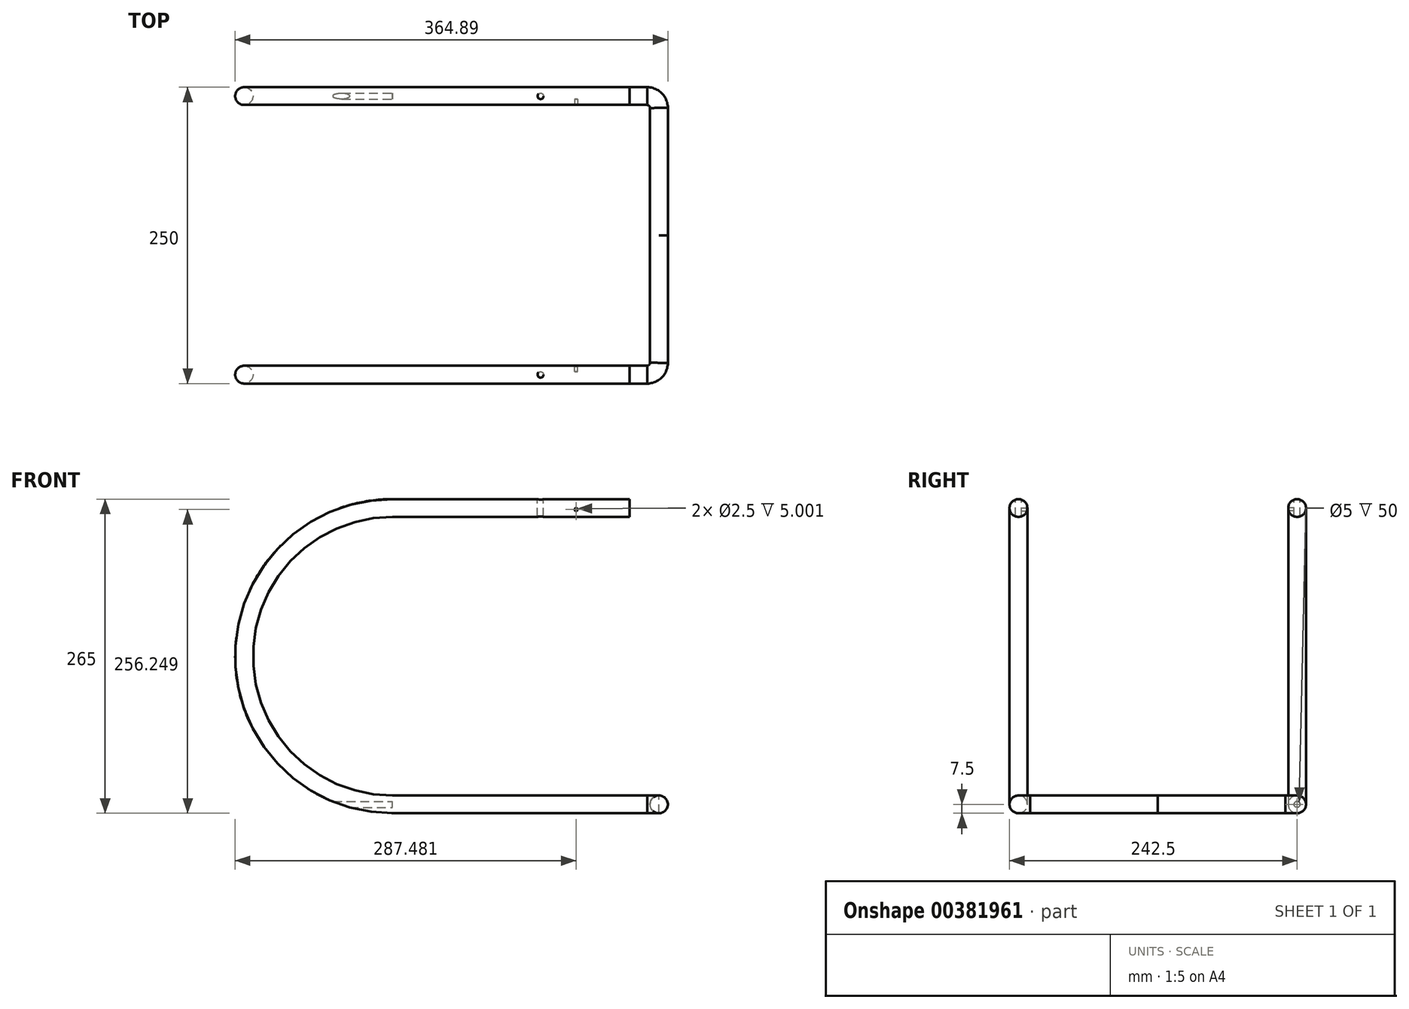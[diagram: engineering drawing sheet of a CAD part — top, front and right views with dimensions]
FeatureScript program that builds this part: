
annotation { "Feature Type Name" : "Feature", "Feature Type Description" : "" }
export const myFeature = defineFeature(function(context is Context, id is Id, definition is map)
    precondition{}
    {
        {
            var Q0;
            Q0=qCreatedBy(makeId("Front.planeOp"),FACE);
            var sketch = newSketch(context, id + "F0", { "sketchPlane" : qUnion([Q0])});
            skLineSegment(sketch, "E0", {"start": v(0, 0) * mm, "end": v(215, 0) * mm});
            skArc(sketch, "E1", {"start": v(0, 250) * mm, "mid": v(-125, 125) * mm, "end": v(0, 0) * mm});
            skLineSegment(sketch, "E2", {"start": v(0, 250) * mm, "end": v(200, 250) * mm});
            skSolve(sketch);
        }
        {
            var Q0;
            Q0=qCreatedBy(makeId("Top.planeOp"),FACE);
            var sketch = newSketch(context, id + "F1", { "sketchPlane" : qUnion([Q0])});
            skLineSegment(sketch, "E3", {"start": v(224.89, -10) * mm, "end": v(224.89, -117.5) * mm});
            skArc(sketch, "E4", {"start": v(224.89, -10) * mm, "mid": v(221.96, -2.93) * mm, "end": v(214.89, 0) * mm});
            skSolve(sketch);
        }
        {
            var Q0;
            Q0=qCreatedBy(makeId("Right.planeOp"),FACE);
            cPlane(context, id + "F2", {"entities" : qUnion([Q0]), "cplaneType" : CPlaneType.OFFSET, "offset" : 215 * mm, "width" : 150 * mm, "height" : 150 * mm});
        }
        {
            var Q0;
            Q0=qCreatedBy(id+"F2.planeOp",FACE);
            var sketch = newSketch(context, id + "F3", { "sketchPlane" : qUnion([Q0])});
            skCircle(sketch, "E5", {"center": v(0, 0) * mm, "radius": 7.5 * mm});
            skSolve(sketch);
        }
        {
            var Q0;
            Q0=makeQuery(id+"F3.imprint","IMPRINT",FACE,{"disambiguationData":[TD([[makeQuery(id+"F3.imprint","IMPRINT",EDGE,{"derivedFrom":sQuery(id+"F3.wireOp",EDGE,"E5")}),1.0]])]});
            var Q1;
            Q1=sQuery(id+"F0.wireOp",EDGE,"E0");
            var Q2;
            Q2=sQuery(id+"F0.wireOp",EDGE,"E1");
            var Q3;
            Q3=sQuery(id+"F0.wireOp",EDGE,"E2");
            sweep(context, id + "F4", {"profiles" : qUnion([Q0]), "path" : qUnion([Q1, Q2, Q3])});
        }
        {
            var Q0;
            Q0=makeQuery(id+"F4.opSweep","CAP_FACE",FACE,{"disambiguationData":[OSD([sQuery(id+"F0.wireOp",VERTEX,"E0.end"),sQuery(id+"F3.wireOp",EDGE,"E5")])],"isStart":true});
            var Q1;
            Q1=sQuery(id+"F1.wireOp",EDGE,"E4");
            var Q2;
            Q2=sQuery(id+"F1.wireOp",EDGE,"E3");
            sweep(context, id + "F5", {"operationType" : NewBodyOperationType.ADD, "profiles" : qUnion([Q0]), "path" : qUnion([Q1, Q2])});
        }
        {
            var Q0;
            Q0=qCreatedBy(makeId("Front.planeOp"),FACE);
            cPlane(context, id + "F6", {"entities" : qUnion([Q0]), "cplaneType" : CPlaneType.OFFSET, "offset" : 117.5 * mm, "width" : 150 * mm, "height" : 150 * mm});
        }
        {
            var Q0;
            Q0=qCreatedBy(makeId("Front.planeOp"),FACE);
            cPlane(context, id + "F7", {"entities" : qUnion([Q0]), "cplaneType" : CPlaneType.OFFSET, "offset" : 7.5 * mm, "width" : 150 * mm, "height" : 150 * mm});
        }
        {
            var Q0;
            Q0=qCreatedBy(id+"F7.planeOp",FACE);
            var sketch = newSketch(context, id + "F8", { "sketchPlane" : qUnion([Q0])});
            skCircle(sketch, "E6", {"center": v(154.98, 248.75) * mm, "radius": 1.25 * mm});
            skSolve(sketch);
        }
        {
            var Q0;
            Q0=qSketchRegion(id+"F8",true);
            extrude(context, id + "F9", {"entities" : qUnion([Q0]), "operationType" : NewBodyOperationType.REMOVE, "oppositeDirection" : true, "depth" : 5 * mm});
        }
        {
            var Q0;
            Q0=makeQuery(id+"F4.opSweep","SWEPT_BODY",BODY,{"disambiguationData":[OSD([sQuery(id+"F0.wireOp",EDGE,"E2"),sQuery(id+"F3.wireOp",EDGE,"E5")])]});
            var Q1;
            Q1=qCreatedBy(id+"F6.planeOp",FACE);
            mirror(context, id + "F10", {"operationType" : NewBodyOperationType.ADD, "entities" : qUnion([Q0]), "mirrorPlane" : qUnion([Q1])});
        }
        {
            var Q0;
            Q0=qCreatedBy(makeId("Right.planeOp"),FACE);
            var sketch = newSketch(context, id + "F11", { "sketchPlane" : qUnion([Q0])});
            skCircle(sketch, "E7", {"center": v(0, 0) * mm, "radius": 2.5 * mm});
            skSolve(sketch);
        }
        {
            var Q0;
            Q0=qSketchRegion(id+"F11",true);
            extrude(context, id + "F12", {"entities" : qUnion([Q0]), "operationType" : NewBodyOperationType.REMOVE, "oppositeDirection" : true, "depth" : 30 * mm});
        }
        {
            var Q0;
            Q0=qCreatedBy(makeId("Right.planeOp"),FACE);
            var sketch = newSketch(context, id + "F13", { "sketchPlane" : qUnion([Q0])});
            skCircle(sketch, "E8", {"center": v(0, 0) * mm, "radius": 2.5 * mm});
            skSolve(sketch);
        }
        {
            var Q0;
            Q0=qSketchRegion(id+"F13",true);
            extrude(context, id + "F14", {"entities" : qUnion([Q0]), "operationType" : NewBodyOperationType.REMOVE, "oppositeDirection" : true, "depth" : 50 * mm});
        }
        {
            var Q0;
            Q0=qCreatedBy(makeId("Top.planeOp"),FACE);
            cPlane(context, id + "F15", {"entities" : qUnion([Q0]), "cplaneType" : CPlaneType.OFFSET, "offset" : 257.5 * mm, "width" : 150 * mm, "height" : 150 * mm});
        }
        {
            var Q0;
            Q0=qCreatedBy(id+"F15.planeOp",FACE);
            var sketch = newSketch(context, id + "F16", { "sketchPlane" : qUnion([Q0])});
            skCircle(sketch, "E9", {"center": v(125, 0) * mm, "radius": 2.5 * mm});
            skCircle(sketch, "E10", {"center": v(125, -235) * mm, "radius": 2.5 * mm});
            skSolve(sketch);
        }
        {
            var Q0;
            Q0=makeQuery(id+"F16.imprint","IMPRINT",FACE,{"disambiguationData":[TD([[makeQuery(id+"F16.imprint","IMPRINT",EDGE,{"derivedFrom":sQuery(id+"F16.wireOp",EDGE,"E9")}),1.0]])]});
            var Q1;
            Q1=makeQuery(id+"F16.imprint","IMPRINT",FACE,{"disambiguationData":[TD([[makeQuery(id+"F16.imprint","IMPRINT",EDGE,{"derivedFrom":sQuery(id+"F16.wireOp",EDGE,"E10")}),1.0]])]});
            extrude(context, id + "F17", {"entities" : qUnion([Q0, Q1]), "operationType" : NewBodyOperationType.REMOVE, "oppositeDirection" : true, "depth" : 15 * mm});
        }
    });
